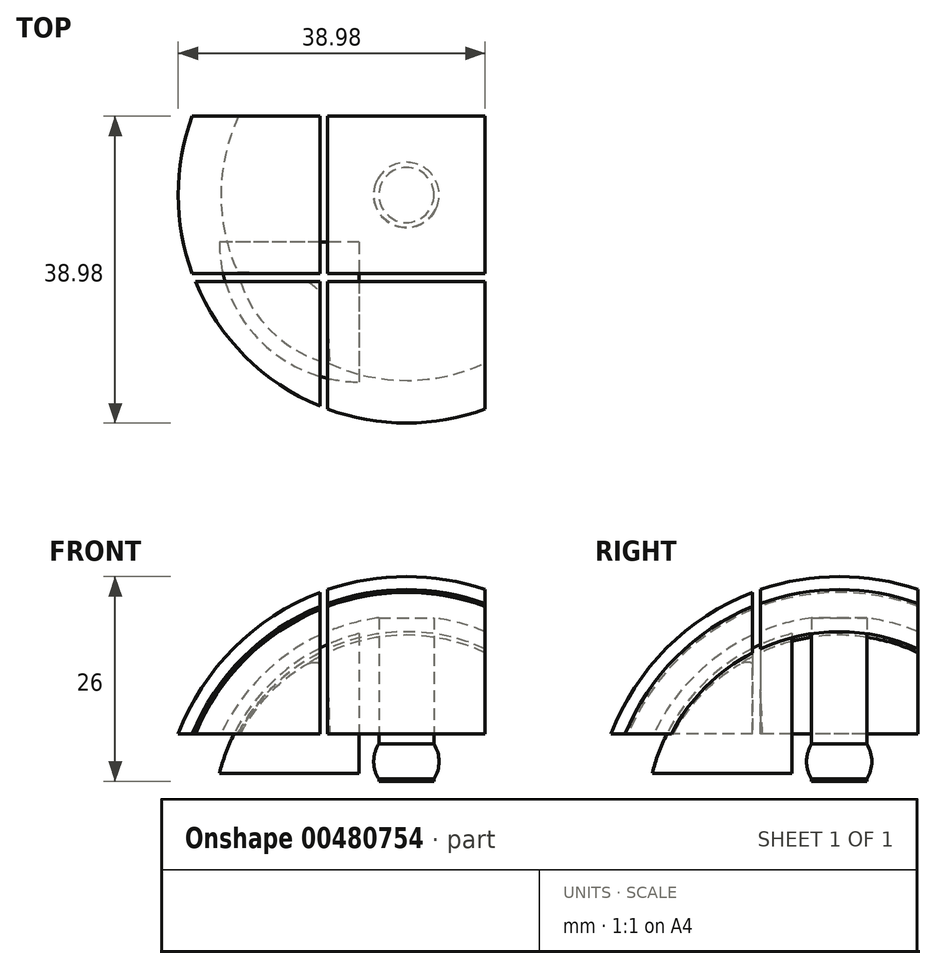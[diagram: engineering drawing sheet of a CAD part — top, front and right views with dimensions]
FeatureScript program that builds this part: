
annotation { "Feature Type Name" : "Feature", "Feature Type Description" : "" }
export const myFeature = defineFeature(function(context is Context, id is Id, definition is map)
    precondition{}
    {
        {
            var Q0;
            Q0=qCreatedBy(makeId("Top.planeOp"),FACE);
            var sketch = newSketch(context, id + "F0", { "sketchPlane" : qUnion([Q0])});
            skLineSegment(sketch, "E0.bottom", {"start": v(-31, 31) * mm, "end": v(31, 31) * mm});
            skLineSegment(sketch, "E0.top", {"start": v(-31, -31) * mm, "end": v(31, -31) * mm});
            skLineSegment(sketch, "E0.left", {"start": v(-31, 31) * mm, "end": v(-31, -31) * mm});
            skLineSegment(sketch, "E0.right", {"start": v(31, 31) * mm, "end": v(31, -31) * mm});
            skSolve(sketch);
        }
        {
            var Q0;
            Q0 = qSketchRegion(id + "F0", true);
            extrude(context, id + "F1", {"entities" : qUnion([Q0]), "endBound" : BoundingType.SYMMETRIC, "depth" : 62 * mm});
        }
        {
            var Q0;
            Q0=makeQuery(id+"F1.opExtrude","CAP_FACE",FACE,{"disambiguationData":[OSD([sQuery(id+"F0.wireOp",EDGE,"E0.bottom"),sQuery(id+"F0.wireOp",EDGE,"E0.top"),sQuery(id+"F0.wireOp",EDGE,"E0.left"),sQuery(id+"F0.wireOp",EDGE,"E0.right")])],"isStart":false});
            var Q1;
            Q1=makeQuery(id+"F1.opExtrude","CAP_FACE",FACE,{"disambiguationData":[OSD([sQuery(id+"F0.wireOp",EDGE,"E0.bottom"),sQuery(id+"F0.wireOp",EDGE,"E0.top"),sQuery(id+"F0.wireOp",EDGE,"E0.left"),sQuery(id+"F0.wireOp",EDGE,"E0.right")])],"isStart":true});
            var Q2;
            Q2=makeQuery(id+"F1.opExtrude","SWEPT_EDGE",EDGE,{"disambiguationData":[OSD([sQuery(id+"F0.wireOp",EDGE,"E0.bottom"),sQuery(id+"F0.wireOp",EDGE,"E0.left")])]});
            var Q3;
            Q3=makeQuery(id+"F1.opExtrude","SWEPT_EDGE",EDGE,{"disambiguationData":[OSD([sQuery(id+"F0.wireOp",EDGE,"E0.top"),sQuery(id+"F0.wireOp",EDGE,"E0.left")])]});
            var Q4;
            Q4=makeQuery(id+"F1.opExtrude","SWEPT_EDGE",EDGE,{"disambiguationData":[OSD([sQuery(id+"F0.wireOp",EDGE,"E0.top"),sQuery(id+"F0.wireOp",EDGE,"E0.right")])]});
            var Q5;
            Q5=makeQuery(id+"F1.opExtrude","SWEPT_EDGE",EDGE,{"disambiguationData":[OSD([sQuery(id+"F0.wireOp",EDGE,"E0.bottom"),sQuery(id+"F0.wireOp",EDGE,"E0.right")])]});
            fillet(context, id + "F2", {"entities" : qUnion([Q0, Q1, Q2, Q3, Q4, Q5]), "radius" : 31 * mm, "tangentPropagation" : true, "allowEdgeOverflow" : false});
        }
        {
            var Q0;
            Q0 = qSketchRegion(id + "F0", true);
            extrude(context, id + "F3", {"entities" : qUnion([Q0]), "operationType" : NewBodyOperationType.REMOVE, "oppositeDirection" : true, "depth" : 31 * mm, "hasSecondDirection" : true, "secondDirectionOppositeDirection" : false, "secondDirectionDepth" : 11 * mm});
        }
        {
            var Q0;
            Q0=qCreatedBy(makeId("Front.planeOp"),FACE);
            var sketch = newSketch(context, id + "F4", { "sketchPlane" : qUnion([Q0])});
            skPoint(sketch, "E1.middle", {"position": v(0, 0) * mm});
            skArc(sketch, "E2", {"start": v(0, -26) * mm, "mid": v(26, 0) * mm, "end": v(0, 26) * mm});
            skLineSegment(sketch, "E3", {"start": v(0, 26) * mm, "end": v(0, -26) * mm});
            skSolve(sketch);
        }
        {
            var Q0;
            Q0 = qSketchRegion(id + "F4", true);
            var Q1;
            Q1=sQuery(id+"F4.wireOp",EDGE,"E3");
            revolve(context, id + "F5", {"operationType" : NewBodyOperationType.REMOVE, "entities" : qUnion([Q0]), "axis" : qUnion([Q1]), "revolveType" : RevolveType.FULL, "oppositeDirection" : true});
        }
        {
            var Q0;
            Q0=qCreatedBy(makeId("Right.planeOp"),FACE);
            cPlane(context, id + "F6", {"entities" : qUnion([Q0]), "cplaneType" : CPlaneType.OFFSET, "offset" : 10 * mm, "width" : 150 * mm, "height" : 150 * mm});
        }
        {
            var Q0;
            Q0=qCreatedBy(id+"F6.planeOp",FACE);
            var sketch = newSketch(context, id + "F7", { "sketchPlane" : qUnion([Q0])});
            skLineSegment(sketch, "E4.bottom", {"start": v(31.5, 31.5) * mm, "end": v(-31.5, 31.5) * mm});
            skLineSegment(sketch, "E4.top", {"start": v(31.5, -31.5) * mm, "end": v(-31.5, -31.5) * mm});
            skLineSegment(sketch, "E4.left", {"start": v(31.5, 31.5) * mm, "end": v(31.5, -31.5) * mm});
            skLineSegment(sketch, "E4.right", {"start": v(-31.5, 31.5) * mm, "end": v(-31.5, -31.5) * mm});
            skPoint(sketch, "E4.middle", {"position": v(0, 0) * mm});
            skSolve(sketch);
        }
        {
            var Q0;
            Q0 = qSketchRegion(id + "F7", true);
            extrude(context, id + "F8", {"entities" : qUnion([Q0]), "operationType" : NewBodyOperationType.REMOVE, "endBound" : BoundingType.THROUGH_ALL, "depth" : 25 * mm});
        }
        {
            var Q0;
            Q0=qCreatedBy(makeId("Right.planeOp"),FACE);
            cPlane(context, id + "F9", {"entities" : qUnion([Q0]), "cplaneType" : CPlaneType.OFFSET, "offset" : 10 * mm, "oppositeDirection" : true, "width" : 150 * mm, "height" : 150 * mm});
        }
        {
            var Q0;
            Q0=qCreatedBy(id+"F9.planeOp",FACE);
            var sketch = newSketch(context, id + "F10", { "sketchPlane" : qUnion([Q0])});
            skLineSegment(sketch, "E5.bottom", {"start": v(31.5, 31.5) * mm, "end": v(-31.5, 31.5) * mm});
            skLineSegment(sketch, "E5.top", {"start": v(31.5, -31.5) * mm, "end": v(-31.5, -31.5) * mm});
            skLineSegment(sketch, "E5.left", {"start": v(31.5, 31.5) * mm, "end": v(31.5, -31.5) * mm});
            skLineSegment(sketch, "E5.right", {"start": v(-31.5, 31.5) * mm, "end": v(-31.5, -31.5) * mm});
            skPoint(sketch, "E5.middle", {"position": v(0, 0) * mm});
            skSolve(sketch);
        }
        {
            var Q0;
            Q0 = qSketchRegion(id + "F10", true);
            extrude(context, id + "F11", {"entities" : qUnion([Q0]), "operationType" : NewBodyOperationType.REMOVE, "oppositeDirection" : true, "depth" : 1 * mm});
        }
        {
            var Q0;
            Q0=qCreatedBy(makeId("Front.planeOp"),FACE);
            cPlane(context, id + "F12", {"entities" : qUnion([Q0]), "cplaneType" : CPlaneType.OFFSET, "offset" : 10 * mm, "width" : 150 * mm, "height" : 150 * mm});
        }
        {
            var Q0;
            Q0=qCreatedBy(id+"F12.planeOp",FACE);
            var sketch = newSketch(context, id + "F13", { "sketchPlane" : qUnion([Q0])});
            skLineSegment(sketch, "E6.bottom", {"start": v(31.5, 31.5) * mm, "end": v(-31.5, 31.5) * mm});
            skLineSegment(sketch, "E6.top", {"start": v(31.5, -31.5) * mm, "end": v(-31.5, -31.5) * mm});
            skLineSegment(sketch, "E6.left", {"start": v(31.5, 31.5) * mm, "end": v(31.5, -31.5) * mm});
            skLineSegment(sketch, "E6.right", {"start": v(-31.5, 31.5) * mm, "end": v(-31.5, -31.5) * mm});
            skPoint(sketch, "E6.middle", {"position": v(0, 0) * mm});
            skSolve(sketch);
        }
        {
            var Q0;
            Q0 = qSketchRegion(id + "F13", true);
            extrude(context, id + "F14", {"entities" : qUnion([Q0]), "operationType" : NewBodyOperationType.REMOVE, "depth" : 1 * mm});
        }
        {
            var Q0;
            Q0=qCreatedBy(makeId("Front.planeOp"),FACE);
            cPlane(context, id + "F15", {"entities" : qUnion([Q0]), "cplaneType" : CPlaneType.OFFSET, "offset" : 10 * mm, "oppositeDirection" : true, "width" : 150 * mm, "height" : 150 * mm});
        }
        {
            var Q0;
            Q0=qCreatedBy(id+"F15.planeOp",FACE);
            var sketch = newSketch(context, id + "F16", { "sketchPlane" : qUnion([Q0])});
            skLineSegment(sketch, "E7.bottom", {"start": v(-31.5, 37.9) * mm, "end": v(31.5, 37.9) * mm});
            skLineSegment(sketch, "E7.top", {"start": v(-31.5, -25.1) * mm, "end": v(31.5, -25.1) * mm});
            skLineSegment(sketch, "E7.left", {"start": v(-31.5, 37.9) * mm, "end": v(-31.5, -25.1) * mm});
            skLineSegment(sketch, "E7.right", {"start": v(31.5, 37.9) * mm, "end": v(31.5, -25.1) * mm});
            skPoint(sketch, "E7.middle", {"position": v(0, 6.4) * mm});
            skSolve(sketch);
        }
        {
            var Q0;
            Q0 = qSketchRegion(id + "F16", true);
            extrude(context, id + "F17", {"entities" : qUnion([Q0]), "operationType" : NewBodyOperationType.REMOVE, "oppositeDirection" : true, "depth" : 25 * mm});
        }
        {
            var Q0;
            Q0=qCreatedBy(makeId("Top.planeOp"),FACE);
            cPlane(context, id + "F18", {"entities" : qUnion([Q0]), "cplaneType" : CPlaneType.OFFSET, "offset" : 5 * mm, "width" : 150 * mm, "height" : 150 * mm});
        }
        {
            var Q0;
            Q0=qCreatedBy(makeId("Top.planeOp"),FACE);
            cPlane(context, id + "F19", {"entities" : qUnion([Q0]), "cplaneType" : CPlaneType.OFFSET, "offset" : 7.5 * mm, "width" : 150 * mm, "height" : 150 * mm});
        }
        {
            var Q0;
            Q0=qCreatedBy(id+"F18.planeOp",FACE);
            var sketch = newSketch(context, id + "F20", { "sketchPlane" : qUnion([Q0])});
            skPoint(sketch, "E8.center.orphan", {"position": v(0.77, 0) * mm});
            skCircle(sketch, "E9", {"center": v(0, 0) * mm, "radius": 3.5 * mm});
            skSolve(sketch);
        }
        {
            var Q0;
            Q0=qCreatedBy(id+"F19.planeOp",FACE);
            var sketch = newSketch(context, id + "F21", { "sketchPlane" : qUnion([Q0])});
            skLineSegment(sketch, "E10", {"start": v(-3.73, 1.83) * mm, "end": v(3.73, -1.83) * mm});
            skArc(sketch, "E11", {"start": v(-3.73, 1.83) * mm, "mid": v(-1.83, -3.73) * mm, "end": v(3.73, -1.83) * mm});
            skSolve(sketch);
        }
        {
            var Q0;
            Q0 = qSketchRegion(id + "F20", true);
            extrude(context, id + "F22", {"entities" : qUnion([Q0]), "operationType" : NewBodyOperationType.ADD, "depth" : 22 * mm});
        }
        {
            var Q0;
            Q0 = qSketchRegion(id + "F21", true);
            var Q1;
            Q1=sQuery(id+"F21.wireOp",EDGE,"E10");
            revolve(context, id + "F23", {"operationType" : NewBodyOperationType.ADD, "entities" : qUnion([Q0]), "axis" : qUnion([Q1]), "revolveType" : RevolveType.FULL});
        }
        {
            var Q0;
            Q0 = qSketchRegion(id + "F20", true);
            extrude(context, id + "F24", {"entities" : qUnion([Q0]), "operationType" : NewBodyOperationType.REMOVE, "oppositeDirection" : true, "depth" : 25 * mm});
        }
        {
            var Q0;
            Q0=qCreatedBy(makeId("Front.planeOp"),FACE);
            cPlane(context, id + "F25", {"entities" : qUnion([Q0]), "cplaneType" : CPlaneType.OFFSET, "offset" : 6 * mm, "width" : 150 * mm, "height" : 150 * mm});
        }
        {
            var Q0;
            Q0=qCreatedBy(id+"F25.planeOp",FACE);
            var sketch = newSketch(context, id + "F26", { "sketchPlane" : qUnion([Q0])});
            skLineSegment(sketch, "E12", {"start": v(0, -24) * mm, "end": v(0, 24) * mm});
            skArc(sketch, "E13", {"start": v(-11, 21.33) * mm, "mid": v(-16.97, 16.97) * mm, "end": v(-21.33, 11) * mm});
            skLineSegment(sketch, "E14", {"start": v(-11, -21.33) * mm, "end": v(-11, 21.33) * mm});
            skLineSegment(sketch, "E15", {"start": v(-11, 11) * mm, "end": v(-21.33, 11) * mm});
            skSolve(sketch);
        }
        {
            var Q0;
            Q0=qCreatedBy(id+"F25.planeOp",FACE);
            var sketch = newSketch(context, id + "F27", { "sketchPlane" : qUnion([Q0])});
            skPoint(sketch, "E16.orphan", {"position": v(0, -23.5) * mm});
            skPoint(sketch, "E17.orphan", {"position": v(0, 23.5) * mm});
            skPoint(sketch, "E18.center.orphan", {"position": v(0, 0) * mm});
            skLineSegment(sketch, "E19", {"start": v(0, 24.5) * mm, "end": v(0, -24.5) * mm});
            skArc(sketch, "E20", {"start": v(-6, 23.75) * mm, "mid": v(-17.32, 17.32) * mm, "end": v(-23.75, 6) * mm});
            skLineSegment(sketch, "E21", {"start": v(0, 6) * mm, "end": v(-23.75, 6) * mm});
            skLineSegment(sketch, "E22", {"start": v(-6, 23.75) * mm, "end": v(-6, 6) * mm});
            skSolve(sketch);
        }
        {
            var Q0;
            Q0 = qSketchRegion(id + "F26", true);
            var Q1;
            Q1=sQuery(id+"F26.wireOp",EDGE,"E14");
            revolve(context, id + "F28", {"operationType" : NewBodyOperationType.ADD, "entities" : qUnion([Q0]), "axis" : qUnion([Q1]), "revolveType" : RevolveType.ONE_DIRECTION, "angle" : 90 * degree});
        }
        {
            var Q0;
            Q0 = qSketchRegion(id + "F27", true);
            var Q1;
            Q1=sQuery(id+"F27.wireOp",EDGE,"E22");
            revolve(context, id + "F29", {"operationType" : NewBodyOperationType.ADD, "entities" : qUnion([Q0]), "axis" : qUnion([Q1]), "revolveType" : RevolveType.ONE_DIRECTION, "oppositeDirection" : true, "angle" : 90 * degree});
        }
    });
